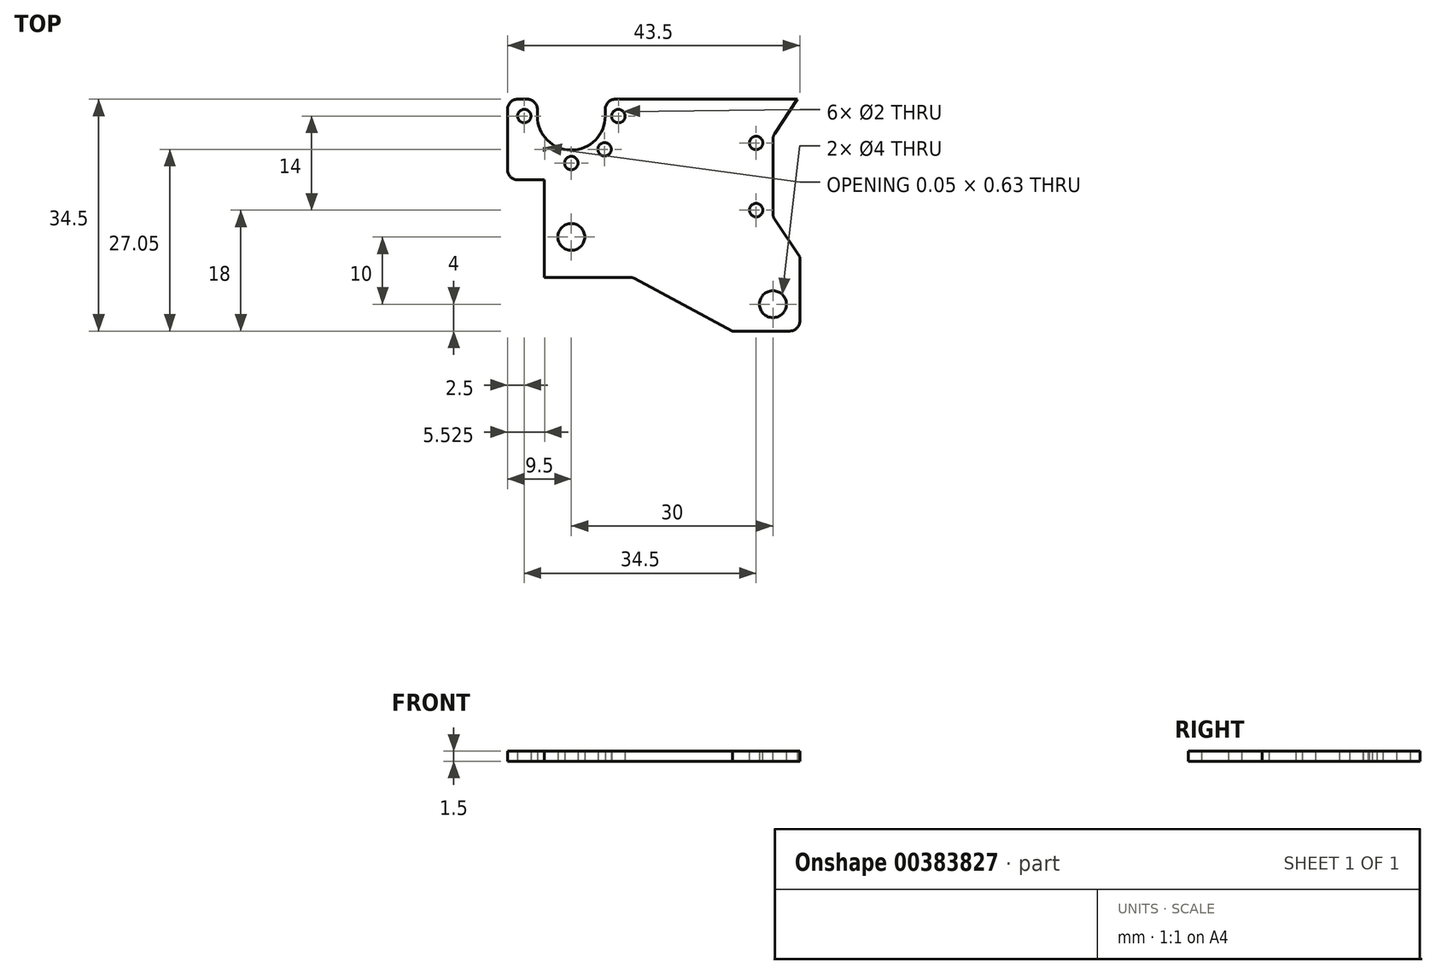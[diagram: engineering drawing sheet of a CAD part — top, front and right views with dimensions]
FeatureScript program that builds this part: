
annotation { "Feature Type Name" : "Feature", "Feature Type Description" : "" }
export const myFeature = defineFeature(function(context is Context, id is Id, definition is map)
    precondition{}
    {
        {
            var Q0;
            Q0=qCreatedBy(makeId("Top.planeOp"),FACE);
            var sketch = newSketch(context, id + "F0", { "sketchPlane" : qUnion([Q0])});
            skLineSegment(sketch, "E0.bottom", {"start": v(19, 17.25) * mm, "end": v(-19, 17.25) * mm});
            skLineSegment(sketch, "E0.top", {"start": v(19, -17.25) * mm, "end": v(-19, -17.25) * mm});
            skLineSegment(sketch, "E0.left", {"start": v(19, 17.25) * mm, "end": v(19, -17.25) * mm});
            skLineSegment(sketch, "E0.right", {"start": v(-19, 17.25) * mm, "end": v(-19, -17.25) * mm});
            skPoint(sketch, "E0.middle", {"position": v(0, 0) * mm});
            skCircle(sketch, "E1", {"center": v(15, -13.25) * mm, "radius": 2 * mm});
            skPoint(sketch, "E2.center", {"position": v(-15, -3.25) * mm});
            skCircle(sketch, "E3", {"center": v(-15, -3.25) * mm, "radius": 2 * mm});
            skArc(sketch, "E4", {"start": v(-20.05, 14.75) * mm, "mid": v(-15, 9.7) * mm, "end": v(-9.95, 14.75) * mm});
            skCircle(sketch, "E5", {"center": v(-8, 14.75) * mm, "radius": 1 * mm});
            skCircle(sketch, "E6.4.0", {"center": v(-22, 14.75) * mm, "radius": 1 * mm});
            skCircle(sketch, "E6.5.0", {"center": v(-19.95, 9.8) * mm, "radius": 1 * mm});
            skCircle(sketch, "E6.6.0", {"center": v(-15, 7.75) * mm, "radius": 1 * mm});
            skCircle(sketch, "E6.7.0", {"center": v(-10.05, 9.8) * mm, "radius": 1 * mm});
            skLineSegment(sketch, "E7.bottom", {"start": v(-19, 17.25) * mm, "end": v(-24.5, 17.25) * mm});
            skLineSegment(sketch, "E7.top", {"start": v(-19, 5.25) * mm, "end": v(-24.5, 5.25) * mm});
            skLineSegment(sketch, "E7.left", {"start": v(-19, 17.25) * mm, "end": v(-19, 5.25) * mm});
            skLineSegment(sketch, "E7.right", {"start": v(-24.5, 17.25) * mm, "end": v(-24.5, 5.25) * mm});
            skLineSegment(sketch, "E8", {"start": v(-9.95, 14.75) * mm, "end": v(-9.95, 17.25) * mm});
            skLineSegment(sketch, "E9", {"start": v(-20.05, 14.75) * mm, "end": v(-20.05, 17.25) * mm});
            skLineSegment(sketch, "E10.bottom", {"start": v(19, 17.25) * mm, "end": v(-5.5, 17.25) * mm});
            skLineSegment(sketch, "E10.top", {"start": v(19, 28.75) * mm, "end": v(-5.5, 28.75) * mm});
            skLineSegment(sketch, "E10.left", {"start": v(19, 17.25) * mm, "end": v(19, 28.75) * mm});
            skLineSegment(sketch, "E10.right", {"start": v(-5.5, 17.25) * mm, "end": v(-5.5, 28.75) * mm});
            skCircle(sketch, "E11", {"center": v(15, 24.75) * mm, "radius": 2 * mm});
            skLineSegment(sketch, "E12", {"start": v(-24.5, 5.25) * mm, "end": v(-19, -17.25) * mm});
            skLineSegment(sketch, "E13", {"start": v(-5.5, 17.25) * mm, "end": v(6.75, 28.75) * mm});
            skSolve(sketch);
        }
        {
            var Q0;
            Q0=makeQuery(id+"F0.imprint","IMPRINT",FACE,{"disambiguationData":[TD([[makeQuery(id+"F0.imprint","IMPRINT",EDGE,{"derivedFrom":sQuery(id+"F0.wireOp",EDGE,"E6.4.0")}),-1.0]])]});
            var Q1;
            Q1=makeQuery(id+"F0.imprint","IMPRINT",FACE,{"disambiguationData":[TD([[makeQuery(id+"F0.imprint","IMPRINT",EDGE,{"derivedFrom":sQuery(id+"F0.wireOp",EDGE,"E0.top")}),-1.0]])]});
            var Q2;
            Q2=makeQuery(id+"F0.imprint","IMPRINT",FACE,{"disambiguationData":[TD([[makeQuery(id+"F0.imprint","IMPRINT",EDGE,{"derivedFrom":sQuery(id+"F0.wireOp",EDGE,"E10.bottom")}),-1.0]])]});
            var Q3;
            Q3=makeQuery(id+"F0.imprint","IMPRINT",FACE,{"disambiguationData":[TD([[makeQuery(id+"F0.imprint","IMPRINT",EDGE,{"derivedFrom":sQuery(id+"F0.wireOp",EDGE,"E0.right")}),-1.0]])]});
            extrude(context, id + "F1", {"entities" : qUnion([Q0, Q1, Q2, Q3]), "depth" : 1.5 * mm});
        }
        {
            var Q0;
            Q0=makeQuery(id+"Fbsrll1mkTp2Ove_1.boolean.opBoolean","MERGE",FACE,{"derivedFrom":[makeQuery(id+"F1.opExtrude","CAP_FACE",FACE,{"disambiguationData":[OSD([sQuery(id+"F0.wireOp",EDGE,"E0.bottom"),sQuery(id+"F0.wireOp",EDGE,"E0.top"),sQuery(id+"F0.wireOp",EDGE,"E0.left"),sQuery(id+"F0.wireOp",EDGE,"E0.right"),sQuery(id+"F0.wireOp",EDGE,"E1"),sQuery(id+"F0.wireOp",EDGE,"E2.2.0"),sQuery(id+"F0.wireOp",EDGE,"E2.3.0"),sQuery(id+"F0.wireOp",EDGE,"E2.4.0"),sQuery(id+"F0.wireOp",EDGE,"E2.5.0"),sQuery(id+"F0.wireOp",EDGE,"E2.6.0"),sQuery(id+"F0.wireOp",EDGE,"65AQZXP9-bqzE-Elh8-uicy-LzplK5Qiw1Dx"),sQuery(id+"F0.wireOp",EDGE,"mMi8jfMq-btWB-gm89-F0K3-MUfdqZMmn9qr"),sQuery(id+"F0.wireOp",EDGE,"1bf6e803-1c66-4d62-a9b5-8abf57308ba9.trimOffspring")])],"isStart":false}),makeQuery(id+"Fbsrll1mkTp2Ove_1.opExtrude","CAP_FACE",FACE,{"disambiguationData":[OSD([sQuery(id+"FltwxiSWxAxMOBe_1.wireOp",EDGE,"hgSAMgcj-rSTU-ZnGC-UjKL-LI2vJDLEC9Sp.bottom"),sQuery(id+"FltwxiSWxAxMOBe_1.wireOp",EDGE,"hgSAMgcj-rSTU-ZnGC-UjKL-LI2vJDLEC9Sp.top"),sQuery(id+"FltwxiSWxAxMOBe_1.wireOp",EDGE,"hgSAMgcj-rSTU-ZnGC-UjKL-LI2vJDLEC9Sp.left"),sQuery(id+"FltwxiSWxAxMOBe_1.wireOp",EDGE,"hgSAMgcj-rSTU-ZnGC-UjKL-LI2vJDLEC9Sp.right")])],"isStart":true})]});
            var sketch = newSketch(context, id + "F2", { "sketchPlane" : qUnion([Q0])});
            skLineSegment(sketch, "E14", {"start": v(-20.96, -9.25) * mm, "end": v(-5.96, -9.25) * mm});
            skLineSegment(sketch, "E15", {"start": v(-5.96, -9.25) * mm, "end": v(9, -17.25) * mm});
            skCircle(sketch, "E16.0", {"center": v(15, -13.25) * mm, "radius": 2 * mm, "construction": true});
            skLineSegment(sketch, "E17", {"start": v(19, 17.75) * mm, "end": v(15, 11.75) * mm});
            skLineSegment(sketch, "E18", {"start": v(15, 11.75) * mm, "end": v(15, 5.75) * mm});
            skLineSegment(sketch, "E19", {"start": v(15, 5.75) * mm, "end": v(19, 5.75) * mm, "construction": true});
            skLineSegment(sketch, "E20.MirrorCS", {"start": v(15, -0.25) * mm, "end": v(15, 5.75) * mm});
            skLineSegment(sketch, "E21.MirrorCS", {"start": v(19, -6.25) * mm, "end": v(15, -0.25) * mm});
            skLineSegment(sketch, "E22", {"start": v(19, 17.75) * mm, "end": v(19, -6.25) * mm});
            skCircle(sketch, "E23.0", {"center": v(-15, -3.25) * mm, "radius": 2 * mm, "construction": true});
            skCircle(sketch, "E24.0", {"center": v(15, 24.75) * mm, "radius": 2 * mm, "construction": true});
            skCircle(sketch, "E25", {"center": v(12.5, 10.75) * mm, "radius": 1 * mm});
            skCircle(sketch, "E26.0.1.0", {"center": v(12.5, 0.75) * mm, "radius": 1 * mm});
            skLineSegment(sketch, "E26.direction1", {"start": v(12.5, 10.75) * mm, "end": v(35, 10.75) * mm, "construction": true});
            skLineSegment(sketch, "E26.direction2", {"start": v(12.5, 10.75) * mm, "end": v(12.5, 0.75) * mm, "construction": true});
            skCircle(sketch, "E27", {"center": v(0, 2) * mm, "radius": 5 * mm, "construction": true});
            skSolve(sketch);
        }
        {
            var Q0;
            Q0=qSketchRegion(id+"F2",true);
            var Q1;
            {var subQ0=sQuery(id+"F2.wireOp",EDGE,"E14");Q1=makeQuery(id+"F2.imprint","IMPRINT",FACE,{"disambiguationData":[TD([[makeQuery(id+"F2.imprint","IMPRINT",EDGE,{"derivedFrom":subQ0}),-1.0]])]});}
            var Q2;
            Q2=makeQuery(id+"F4N7lcSIpfRVr36_3.opPattern","COPY",FACE,{"derivedFrom":makeQuery(id+"Fbsrll1mkTp2Ove_1.boolean.opBoolean","MERGE",FACE,{"derivedFrom":[makeQuery(id+"F1.opExtrude","CAP_FACE",FACE,{"disambiguationData":[OSD([sQuery(id+"F0.wireOp",EDGE,"E0.bottom"),sQuery(id+"F0.wireOp",EDGE,"E0.top"),sQuery(id+"F0.wireOp",EDGE,"E0.left"),sQuery(id+"F0.wireOp",EDGE,"E0.right"),sQuery(id+"F0.wireOp",EDGE,"E1"),sQuery(id+"F0.wireOp",EDGE,"E2.2.0"),sQuery(id+"F0.wireOp",EDGE,"E2.3.0"),sQuery(id+"F0.wireOp",EDGE,"E2.4.0"),sQuery(id+"F0.wireOp",EDGE,"E2.5.0"),sQuery(id+"F0.wireOp",EDGE,"E2.6.0"),sQuery(id+"F0.wireOp",EDGE,"65AQZXP9-bqzE-Elh8-uicy-LzplK5Qiw1Dx"),sQuery(id+"F0.wireOp",EDGE,"mMi8jfMq-btWB-gm89-F0K3-MUfdqZMmn9qr"),sQuery(id+"F0.wireOp",EDGE,"1bf6e803-1c66-4d62-a9b5-8abf57308ba9.trimOffspring")])],"isStart":false}),makeQuery(id+"Fbsrll1mkTp2Ove_1.opExtrude","CAP_FACE",FACE,{"disambiguationData":[OSD([sQuery(id+"FltwxiSWxAxMOBe_1.wireOp",EDGE,"hgSAMgcj-rSTU-ZnGC-UjKL-LI2vJDLEC9Sp.bottom"),sQuery(id+"FltwxiSWxAxMOBe_1.wireOp",EDGE,"hgSAMgcj-rSTU-ZnGC-UjKL-LI2vJDLEC9Sp.top"),sQuery(id+"FltwxiSWxAxMOBe_1.wireOp",EDGE,"hgSAMgcj-rSTU-ZnGC-UjKL-LI2vJDLEC9Sp.left"),sQuery(id+"FltwxiSWxAxMOBe_1.wireOp",EDGE,"hgSAMgcj-rSTU-ZnGC-UjKL-LI2vJDLEC9Sp.right")])],"isStart":true})]}),"instanceName":"1"});
            extrude(context, id + "F3", {"entities" : qUnion([Q0, Q1]), "operationType" : NewBodyOperationType.REMOVE, "endBound" : BoundingType.THROUGH_ALL, "oppositeDirection" : true, "endBoundEntityFace" : qUnion([Q2]), "depth" : 25 * mm});
        }
        {
            var Q0;
            Q0=makeQuery(id+"F3.boolean.opBoolean","COPY",EDGE,{"derivedFrom":makeQuery(id+"F3.opExtrude","SWEPT_EDGE",EDGE,{"disambiguationData":[OSD([sQuery(id+"F0.wireOp",EDGE,"E0.right"),sQuery(id+"F2.wireOp",EDGE,"E14")])]})});
            var Q1;
            Q1=makeQuery(id+"F3.boolean.opBoolean","COPY",EDGE,{"derivedFrom":makeQuery(id+"F3.opExtrude","SWEPT_EDGE",EDGE,{"disambiguationData":[OSD([sQuery(id+"F2.wireOp",EDGE,"E14"),sQuery(id+"F2.wireOp",EDGE,"E15")])]})});
            var Q2;
            Q2=makeQuery(id+"F3.boolean.opBoolean","COPY",EDGE,{"derivedFrom":makeQuery(id+"F3.opExtrude","SWEPT_EDGE",EDGE,{"disambiguationData":[OSD([sQuery(id+"F0.wireOp",EDGE,"E0.top"),sQuery(id+"F2.wireOp",EDGE,"E15")])]})});
            var Q3;
            Q3=makeQuery(id+"F1.opExtrude","SWEPT_EDGE",EDGE,{"disambiguationData":[OSD([sQuery(id+"F0.wireOp",EDGE,"E0.top"),sQuery(id+"F0.wireOp",EDGE,"E0.left")])]});
            var Q4;
            Q4=makeQuery(id+"F3.boolean.opBoolean","COPY",EDGE,{"derivedFrom":makeQuery(id+"F3.opExtrude","SWEPT_EDGE",EDGE,{"disambiguationData":[OSD([sQuery(id+"F0.wireOp",EDGE,"E0.left"),sQuery(id+"F2.wireOp",EDGE,"E17"),sQuery(id+"F2.wireOp",EDGE,"E22")])]})});
            var Q5;
            Q5=makeQuery(id+"F3.boolean.opBoolean","COPY",EDGE,{"derivedFrom":makeQuery(id+"F3.opExtrude","SWEPT_EDGE",EDGE,{"disambiguationData":[OSD([sQuery(id+"F2.wireOp",EDGE,"E17"),sQuery(id+"F2.wireOp",EDGE,"E18")])]})});
            var Q6;
            Q6=makeQuery(id+"F3.boolean.opBoolean","COPY",EDGE,{"derivedFrom":makeQuery(id+"F3.opExtrude","SWEPT_EDGE",EDGE,{"disambiguationData":[OSD([sQuery(id+"F2.wireOp",EDGE,"E20.MirrorCS"),sQuery(id+"F2.wireOp",EDGE,"E21.MirrorCS")])]})});
            var Q7;
            Q7=makeQuery(id+"F3.boolean.opBoolean","COPY",EDGE,{"derivedFrom":makeQuery(id+"F3.opExtrude","SWEPT_EDGE",EDGE,{"disambiguationData":[OSD([sQuery(id+"F0.wireOp",EDGE,"E0.left"),sQuery(id+"F2.wireOp",EDGE,"E21.MirrorCS"),sQuery(id+"F2.wireOp",EDGE,"E22")])]})});
            var Q8;
            Q8=makeQuery(id+"F1.opExtrude","SWEPT_EDGE",EDGE,{"disambiguationData":[OSD([sQuery(id+"F0.wireOp",EDGE,"E7.bottom"),sQuery(id+"F0.wireOp",EDGE,"E7.right")])]});
            var Q9;
            Q9=makeQuery(id+"F1.opExtrude","SWEPT_EDGE",EDGE,{"disambiguationData":[OSD([sQuery(id+"F0.wireOp",EDGE,"E7.bottom"),sQuery(id+"F0.wireOp",EDGE,"E9")])]});
            var Q10;
            Q10=makeQuery(id+"F1.opExtrude","SWEPT_EDGE",EDGE,{"disambiguationData":[OSD([sQuery(id+"F0.wireOp",EDGE,"E0.bottom"),sQuery(id+"F0.wireOp",EDGE,"E8")])]});
            var Q11;
            Q11=makeQuery(id+"F1.opExtrude","SWEPT_EDGE",EDGE,{"disambiguationData":[OSD([sQuery(id+"F0.wireOp",EDGE,"E0.bottom"),sQuery(id+"F0.wireOp",EDGE,"E10.bottom"),sQuery(id+"F0.wireOp",EDGE,"E10.right"),sQuery(id+"F0.wireOp",EDGE,"E13")])]});
            var Q12;
            Q12=makeQuery(id+"F1.opExtrude","SWEPT_EDGE",EDGE,{"disambiguationData":[OSD([sQuery(id+"F0.wireOp",EDGE,"E10.top"),sQuery(id+"F0.wireOp",EDGE,"E13")])]});
            var Q13;
            Q13=makeQuery(id+"F1.opExtrude","SWEPT_EDGE",EDGE,{"disambiguationData":[OSD([sQuery(id+"F0.wireOp",EDGE,"E10.top"),sQuery(id+"F0.wireOp",EDGE,"E10.left")])]});
            var Q14;
            Q14=makeQuery(id+"F1.opExtrude","SWEPT_EDGE",EDGE,{"disambiguationData":[OSD([sQuery(id+"F0.wireOp",EDGE,"E7.top"),sQuery(id+"F0.wireOp",EDGE,"E7.right"),sQuery(id+"F0.wireOp",EDGE,"E12")])]});
            fillet(context, id + "F4", {"entities" : qUnion([Q0, Q1, Q2, Q3, Q4, Q5, Q6, Q7, Q8, Q9, Q10, Q11, Q12, Q13, Q14]), "radius" : 1.5 * mm, "tangentPropagation" : true, "allowEdgeOverflow" : false});
        }
    });
